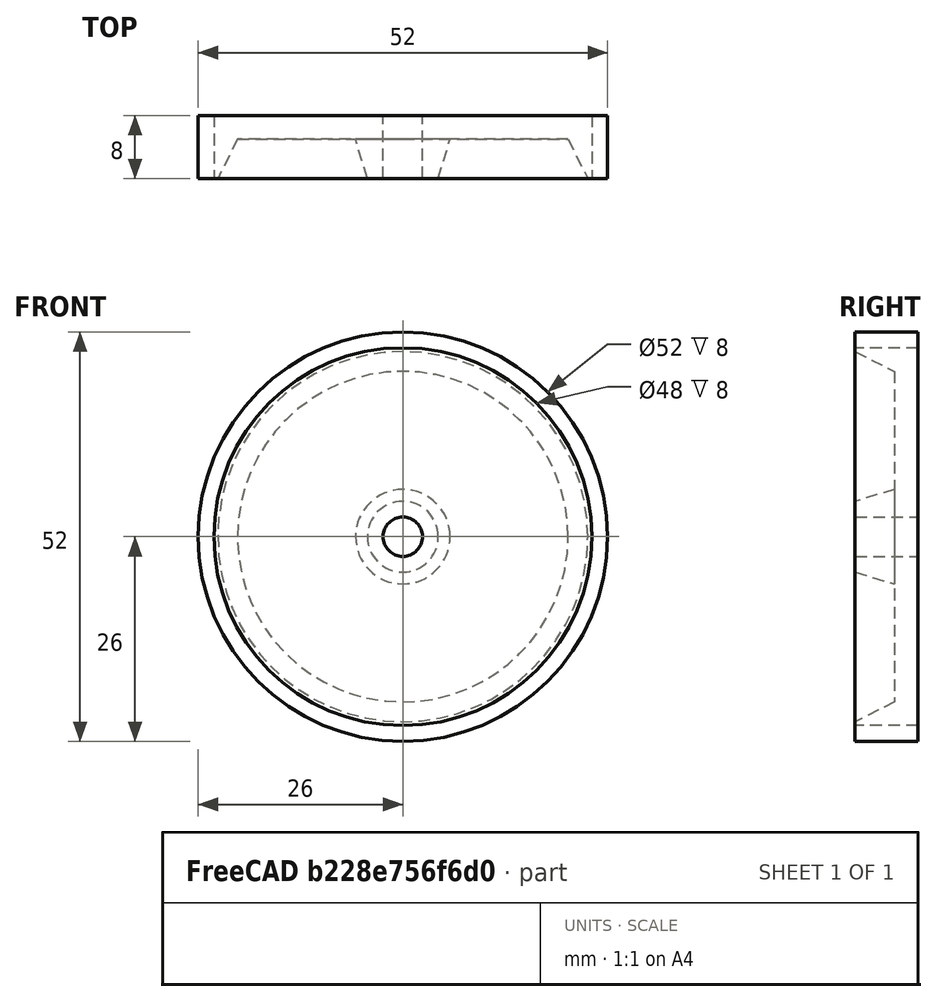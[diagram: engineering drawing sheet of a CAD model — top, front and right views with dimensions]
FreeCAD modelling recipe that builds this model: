
FCSTD DOCUMENT  (FreeCAD 0.16R6704 (Git))
Label: wheel
License: All rights reserved
LicenseURL: http://en.wikipedia.org/wiki/All_rights_reserved
objects: Sketcher::SketchObject×2, Part::Revolution×2, Part::MultiFuse×1
note: 5 computed .brp shape members not serialized (recipe doc carries the construction recipe); baked Part::Feature solids carry a one-line shape summary decoded from their .brp

FEATURE [Sketcher::SketchObject] Sketch
  Placement = pos=(0,0,0) rot=(0.57735,0.57735,0.57735;2.0944rad)
  sketch-geometry (11):
    g0: LineSegment StartX=-8 StartY=24 StartZ=0 EndX=-8 EndY=23.5 EndZ=0
    g1: LineSegment StartX=-8 StartY=23.5 StartZ=0 EndX=-3 EndY=21 EndZ=0
    g2: LineSegment StartX=-3 StartY=21 StartZ=0 EndX=-3 EndY=6 EndZ=0
    g3: LineSegment StartX=-3 StartY=6 StartZ=0 EndX=-8 EndY=4.5 EndZ=0
    g4: LineSegment StartX=-8 StartY=4.5 StartZ=0 EndX=-8 EndY=2.5 EndZ=0
    g5: LineSegment StartX=-8 StartY=2.5 StartZ=0 EndX=0 EndY=2.5 EndZ=0
    g6: LineSegment StartX=0 StartY=2.5 StartZ=0 EndX=0 EndY=24 EndZ=0
    g7: LineSegment StartX=0 StartY=24 StartZ=0 EndX=-8 EndY=24 EndZ=0
    g8: LineSegment [constr] StartX=-3 StartY=21 StartZ=0 EndX=-3 EndY=24 EndZ=0
    g9: LineSegment [constr] StartX=-3 StartY=6 StartZ=0 EndX=-3 EndY=2.5 EndZ=0
    g10: LineSegment [constr] StartX=-3 StartY=6 StartZ=0 EndX=0 EndY=6 EndZ=0
  constraints (33):
    c: Vertical(g0)
    c: Coincident(g0,g1)
    c: Coincident(g1,g2)
    c: Vertical(g2)
    c: Coincident(g2,g3)
    c: Coincident(g3,g4)
    c: Coincident(g4,g5)
    c: Horizontal(g5)
    c: Coincident(g5,g6)
    c: PointOnObject(g6,g-2)
    c: Vertical(g6)
    c: Coincident(g6,g7)
    c: Coincident(g7,g0)
    c: Horizontal(g7)
    c: DistanceY(g6,g6) = 21.5
    c: DistanceX(g5,g5) = 8
    c: DistanceY(g-1,g5) = 2.5
    c: Vertical(g4)
    c: DistanceY(g4,g4) = 2
    c: DistanceY(g0,g0) = 0.5
    c: Coincident(g8,g1)
    c: PointOnObject(g8,g7)
    c: Vertical(g8)
    c: Coincident(g9,g2)
    c: PointOnObject(g9,g5)
    c: Vertical(g9)
    c: Coincident(g10,g2)
    c: PointOnObject(g10,g6)
    c: Horizontal(g10)
    c: DistanceY(g8,g8) = 3
    c: DistanceX(g10,g10) = 3
    c: DistanceY(g9,g9) = 3.5
    c: DistanceX(g0,g6) = 8
FEATURE [Part::Revolution] Revolve  label="ホイール"
  Angle = 360
  Axis = (0,1,0)
  Base = (0,0,0)
  Solid = false
  Source = -> Sketch
FEATURE [Sketcher::SketchObject] Sketch001
  Placement = pos=(0,0,0) rot=(0.57735,0.57735,0.57735;2.0944rad)
  sketch-geometry (4):
    g0: LineSegment StartX=-8 StartY=26 StartZ=0 EndX=0 EndY=26 EndZ=0
    g1: LineSegment StartX=0 StartY=26 StartZ=0 EndX=0 EndY=24 EndZ=0
    g2: LineSegment StartX=0 StartY=24 StartZ=0 EndX=-8 EndY=24 EndZ=0
    g3: LineSegment StartX=-8 StartY=24 StartZ=0 EndX=-8 EndY=26 EndZ=0
  constraints (12):
    c: Coincident(g0,g1)
    c: Coincident(g1,g2)
    c: Coincident(g2,g3)
    c: Coincident(g3,g0)
    c: Horizontal(g0)
    c: Horizontal(g2)
    c: Vertical(g1)
    c: Vertical(g3)
    c: PointOnObject(g1,g-2)
    c: DistanceY(g-1,g1) = 24
    c: DistanceY(g1,g1) = 2
    c: DistanceX(g0,g0) = 8
FEATURE [Part::Revolution] Revolve001  label="タイヤ"
  Angle = 360
  Axis = (0,1,0)
  Base = (0,0,0)
  Solid = false
  Source = -> Sketch001
FEATURE [Part::MultiFuse] Fusion
  Shapes = -> [Revolve,Revolve001]
